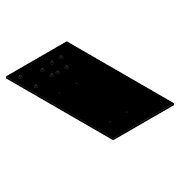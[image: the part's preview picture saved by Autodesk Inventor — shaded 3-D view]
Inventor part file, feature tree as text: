
AUTODESK INVENTOR PART (.ipt)
format: ipt  version: 2020 (Build 240168000, 168)  size: 333,312 bytes
history: native  units: mm
features: projected_geometry x9, extrude x6, sketch x6, chamfer x1
ambient origin geometry x8: Origin, YZ Plane, XZ Plane, XY Plane, X Axis, Y Axis, Z Axis, Center Point
bodies: Solid1 (feature_tree)
feature tree (22):
  extrude  "Extrusion1"  Depth=5.0mm
  extrude  "Extrusion2"  Depth=5.0mm
  extrude  "Extrusion3"  TaperAngle=0.0deg  [1 undecoded]
  extrude  "Extrusion4"  Depth=150.0mm
  extrude  "Extrusion5"  Depth=32.0mm
  extrude  "Extrusion6"  Depth=4.0mm
  chamfer  "Chamfer1"  Distance=113.0mm
  sketch  "Sketch1"  dims[d0=319.6mm d1=5.0mm]
  sketch  "Sketch2"  dims[d2=180.9mm d3=0.0mm d4=5.0mm]
  projected_geometry  "Projected Loop1"
  sketch  "Sketch3"  dims[d5=5.0mm d6=0.0mm]
  projected_geometry  "Projected Loop2"
  projected_geometry  "Projected Loop3"
  projected_geometry  "Projected Loop4"
  projected_geometry  "Projected Loop5"
  sketch  "Sketch4"  dims[d7=0.0mm d8=150.0mm]
  sketch  "Sketch5"  dims[d9=50.0mm d10=32.0mm]
  sketch  "Sketch6"  dims[d11=32.0mm d12=215.0mm d13=113.0mm d14=2.54mm d15=3.592102mm d16=32.766mm d17=3.175mm d18=3.175mm d19=3.592102mm d20=12.954mm d21=66.04mm d22=53.34mm d23=66.04mm d24=7.62mm d27=17.78mm d28=2.54mm d29=5.08mm d31=2.556702mm d32=9.5mm d33=12.04mm d34=20.2mm d35=8.8mm d36=8.5mm d37=8.5mm d38=15.38mm d39=15.38mm d40=11.12mm d41=8.0mm d42=0.5mm d43=0.5mm d44=3.5mm d45=3.5mm d46=0.1mm d47=0.1mm d48=0.56mm d49=0.46mm d50=0.46mm d51=0.56mm d52=7.75mm d53=4.75mm d54=135.0deg d55=135.0deg d56=135.0deg d58=0.2mm d59=10.0mm d60=5.0mm d61=15.63mm d62=2.9mm d63=2.9mm d64=2.9mm d65=2.9mm d66=5.0mm d67=5.0mm d68=5.0mm d69=5.0mm d70=4.0mm d71=0.0mm d72=4.0mm d73=0.0mm d74=5.0mm d75=5.0mm d76=0.0mm d77=0.0mm d78=150.0mm d79=50.0mm d80=32.0mm d81=32.0mm d82=215.0mm d83=113.0mm d84=2.54mm d85=3.592102mm d86=32.766mm d87=3.175mm d88=3.175mm d89=3.592102mm d90=12.954mm d91=66.04mm d92=53.34mm d93=66.04mm d94=7.62mm d95=2.54mm d96=2.54mm d97=17.78mm d98=2.54mm d99=5.08mm d100=15.223298mm d101=2.556702mm d102=9.5mm d103=12.04mm d104=20.2mm d105=8.8mm d106=8.5mm d107=8.5mm d108=15.38mm d109=15.38mm d110=11.12mm d111=8.0mm d112=0.5mm d113=0.5mm d114=3.5mm d115=3.5mm d116=0.1mm d117=0.1mm d118=0.56mm d119=0.46mm d120=0.46mm d121=0.56mm d122=7.75mm d123=4.75mm d124=135.0deg d125=135.0deg d126=135.0deg d127=13.97mm d128=0.2mm d129=10.0mm d130=5.0mm d131=15.63mm d132=2.9mm d133=2.9mm d134=2.9mm d135=2.9mm d136=5.0mm d137=5.0mm d138=5.0mm d139=5.0mm d140=3.5mm d141=3.5mm d142=3.5mm d143=3.5mm d144=0.0mm d145=0.0mm d146=17.6mm d147=18.870001mm d148=0.89mm d149=73.0mm d150=22.0899mm d151=46.2836mm d152=22.0899mm d153=46.2836mm d154=2.6mm d155=6.1mm d156=2.1mm d157=6.1mm d158=22.0899mm d159=46.2836mm d160=22.0899mm d161=46.2836mm d162=2.6mm d163=6.1mm d164=2.1mm d165=6.1mm d166=74.0mm d167=0.0mm d168=0.0mm d169=10.0mm d170=5.0mm d171=2.9mm d172=5.0mm d173=2.9mm d174=5.0mm d175=2.9mm d176=5.0mm d177=2.9mm d178=5.0mm d179=4.0mm d180=0.0mm d181=4.0mm d182=0.0mm d183=2.0mm d184=2.0mm d185=45.0deg]
  projected_geometry  "Projected Loop6"
  projected_geometry  "Projected Loop7"
  projected_geometry  "Projected Loop8"
  projected_geometry  "Projected Loop9"
note: 1 required parameter value undecoded (feature->parameter linkage not recoverable at this tier; creation-order binding heuristic only, values carry confidence <= 0.55)
